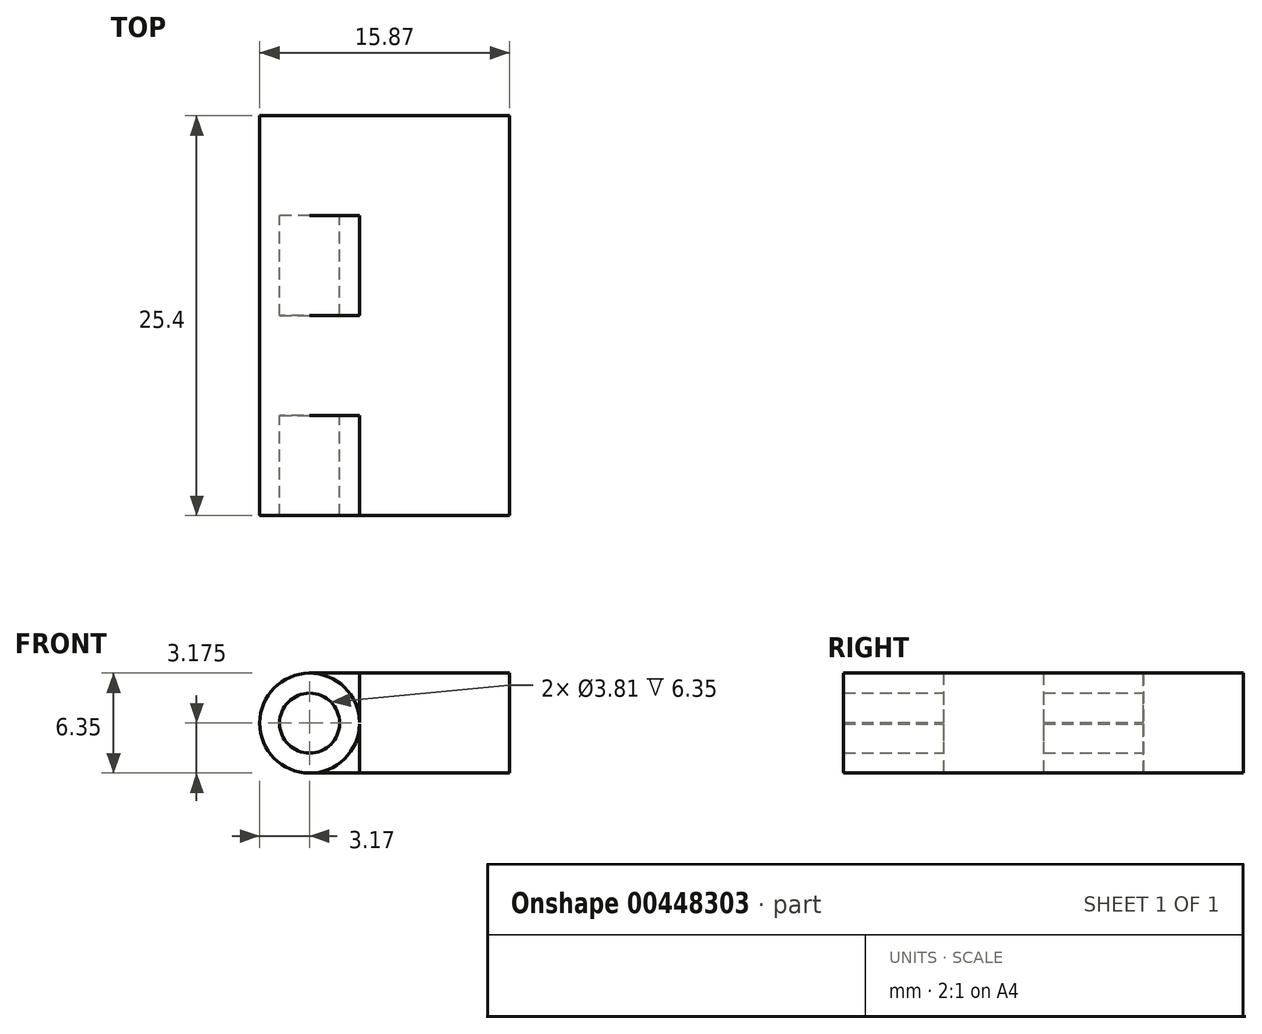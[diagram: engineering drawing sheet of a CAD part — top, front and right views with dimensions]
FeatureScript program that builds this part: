
annotation { "Feature Type Name" : "Feature", "Feature Type Description" : "" }
export const myFeature = defineFeature(function(context is Context, id is Id, definition is map)
    precondition{}
    {
        {
            var Q0;
            Q0=qCreatedBy(makeId("Top.planeOp"),FACE);
            var sketch = newSketch(context, id + "F0", { "sketchPlane" : qUnion([Q0])});
            skLineSegment(sketch, "E0.bottom", {"start": v(6.35, -12.7) * mm, "end": v(-6.35, -12.7) * mm});
            skLineSegment(sketch, "E0.top", {"start": v(6.35, 12.7) * mm, "end": v(-6.35, 12.7) * mm});
            skLineSegment(sketch, "E0.left", {"start": v(6.35, -12.7) * mm, "end": v(6.35, 12.7) * mm});
            skLineSegment(sketch, "E0.right", {"start": v(-6.35, -12.7) * mm, "end": v(-6.35, 12.7) * mm});
            skPoint(sketch, "E0.middle", {"position": v(0, 0) * mm});
            skSolve(sketch);
        }
        {
            var Q0;
            Q0=qSketchRegion(id+"F0",true);
            extrude(context, id + "F1", {"entities" : qUnion([Q0]), "depth" : 6.35 * mm});
        }
        {
            var Q0;
            Q0=makeQuery(id+"F1.opExtrude","SWEPT_FACE",FACE,{"disambiguationData":[OSD([sQuery(id+"F0.wireOp",EDGE,"E0.top")])]});
            var sketch = newSketch(context, id + "F2", { "sketchPlane" : qUnion([Q0])});
            skCircle(sketch, "E1", {"center": v(-6.35, 3.18) * mm, "radius": 3.17 * mm});
            skCircle(sketch, "E2", {"center": v(-6.35, 3.18) * mm, "radius": 1.9 * mm});
            skCircle(sketch, "E3.MirrorC", {"center": v(6.35, 3.18) * mm, "radius": 3.17 * mm});
            skCircle(sketch, "E4.MirrorC", {"center": v(6.35, 3.18) * mm, "radius": 1.9 * mm});
            skSolve(sketch);
        }
        {
            var Q0;
            {var subQ1=sQuery(id+"F0.wireOp",EDGE,"E0.top");var subQ2=makeQuery(id+"F1.opExtrude","SWEPT_EDGE",EDGE,{"disambiguationData":[OSD([subQ1,sQuery(id+"F0.wireOp",EDGE,"E0.right")])]});var subQ5=sQuery(id+"F2.wireOp",EDGE,"E4.MirrorC");var subQ7=makeQuery(id+"F2.imprint","INTERSECT",VERTEX,{"disambiguationData":[OD(0.0)],"derivedFrom":[subQ2,subQ5]});Q0=makeQuery(id+"F2.imprint","IMPRINT",FACE,{"disambiguationData":[TD([[makeQuery(id+"F2.imprint","IMPRINT",EDGE,{"disambiguationData":[TD([[subQ7,1.0]])],"derivedFrom":subQ5}),1.0]])]});}
            var Q1;
            {var subQ1=sQuery(id+"F0.wireOp",EDGE,"E0.top");var subQ2=makeQuery(id+"F1.opExtrude","SWEPT_EDGE",EDGE,{"disambiguationData":[OSD([subQ1,sQuery(id+"F0.wireOp",EDGE,"E0.left")])]});var subQ5=sQuery(id+"F2.wireOp",EDGE,"E2");var subQ7=makeQuery(id+"F2.imprint","INTERSECT",VERTEX,{"disambiguationData":[OD(0.0)],"derivedFrom":[subQ2,subQ5]});Q1=makeQuery(id+"F2.imprint","IMPRINT",FACE,{"disambiguationData":[TD([[makeQuery(id+"F2.imprint","IMPRINT",EDGE,{"disambiguationData":[TD([[subQ7,-1.0]])],"derivedFrom":subQ5}),-1.0]])]});}
            var Q2;
            {var subQ1=sQuery(id+"F0.wireOp",EDGE,"E0.top");var subQ2=makeQuery(id+"F1.opExtrude","SWEPT_EDGE",EDGE,{"disambiguationData":[OSD([subQ1,sQuery(id+"F0.wireOp",EDGE,"E0.right")])]});var subQ5=sQuery(id+"F2.wireOp",EDGE,"E4.MirrorC");var subQ6=makeQuery(id+"F2.imprint","INTERSECT",VERTEX,{"disambiguationData":[OD(0.0)],"derivedFrom":[subQ2,subQ5]});Q2=makeQuery(id+"F2.imprint","IMPRINT",FACE,{"disambiguationData":[TD([[makeQuery(id+"F2.imprint","IMPRINT",EDGE,{"disambiguationData":[TD([[subQ6,-1.0]])],"derivedFrom":subQ5}),1.0]])]});}
            var Q3;
            {var subQ0=sQuery(id+"F2.wireOp",EDGE,"E2");var subQ1=makeQuery(id+"F1.opExtrude","SWEPT_EDGE",EDGE,{"disambiguationData":[OSD([sQuery(id+"F0.wireOp",EDGE,"E0.top"),sQuery(id+"F0.wireOp",EDGE,"E0.left")])]});var subQ2=makeQuery(id+"F2.imprint","INTERSECT",VERTEX,{"disambiguationData":[OD(0.0)],"derivedFrom":[subQ1,subQ0]});Q3=makeQuery(id+"F2.imprint","IMPRINT",FACE,{"disambiguationData":[TD([[makeQuery(id+"F2.imprint","IMPRINT",EDGE,{"disambiguationData":[TD([[subQ2,-1.0]])],"derivedFrom":subQ0}),1.0]])]});}
            extrude(context, id + "F3", {"entities" : qUnion([Q0, Q1, Q2, Q3]), "operationType" : NewBodyOperationType.ADD, "oppositeDirection" : true, "depth" : 25.4 * mm});
        }
        {
            var Q0;
            {var subQ0=sQuery(id+"F2.wireOp",EDGE,"E2");var subQ1=makeQuery(id+"F1.opExtrude","SWEPT_EDGE",EDGE,{"disambiguationData":[OSD([sQuery(id+"F0.wireOp",EDGE,"E0.top"),sQuery(id+"F0.wireOp",EDGE,"E0.left")])]});var subQ2=makeQuery(id+"F2.imprint","INTERSECT",VERTEX,{"disambiguationData":[OD(0.0)],"derivedFrom":[subQ1,subQ0]});Q0=makeQuery(id+"F2.imprint","IMPRINT",FACE,{"disambiguationData":[TD([[makeQuery(id+"F2.imprint","IMPRINT",EDGE,{"disambiguationData":[TD([[subQ2,1.0]])],"derivedFrom":subQ0}),1.0]])]});}
            var Q1;
            {var subQ0=sQuery(id+"F2.wireOp",EDGE,"E4.MirrorC");var subQ1=makeQuery(id+"F1.opExtrude","SWEPT_EDGE",EDGE,{"disambiguationData":[OSD([sQuery(id+"F0.wireOp",EDGE,"E0.top"),sQuery(id+"F0.wireOp",EDGE,"E0.right")])]});var subQ2=makeQuery(id+"F2.imprint","INTERSECT",VERTEX,{"disambiguationData":[OD(0.0)],"derivedFrom":[subQ1,subQ0]});Q1=makeQuery(id+"F2.imprint","IMPRINT",FACE,{"disambiguationData":[TD([[makeQuery(id+"F2.imprint","IMPRINT",EDGE,{"disambiguationData":[TD([[subQ2,-1.0]])],"derivedFrom":subQ0}),-1.0]])]});}
            extrude(context, id + "F4", {"entities" : qUnion([Q0, Q1]), "operationType" : NewBodyOperationType.REMOVE, "oppositeDirection" : true, "depth" : 25.4 * mm});
        }
        {
            var Q0;
            Q0=makeQuery(id+"F1.opExtrude","CAP_FACE",FACE,{"disambiguationData":[OSD([sQuery(id+"F0.wireOp",EDGE,"E0.bottom"),sQuery(id+"F0.wireOp",EDGE,"E0.top"),sQuery(id+"F0.wireOp",EDGE,"E0.left"),sQuery(id+"F0.wireOp",EDGE,"E0.right")])],"isStart":true});
            var sketch = newSketch(context, id + "F5", { "sketchPlane" : qUnion([Q0])});
            skPoint(sketch, "E5.middle", {"position": v(6.35, 9.52) * mm});
            skLineSegment(sketch, "E6.MirrorCS", {"start": v(3.18, -12.7) * mm, "end": v(3.18, -6.35) * mm});
            skLineSegment(sketch, "E7.MirrorCS", {"start": v(9.53, -12.7) * mm, "end": v(9.53, -6.35) * mm});
            skLineSegment(sketch, "E8.MirrorCS", {"start": v(9.52, -12.7) * mm, "end": v(3.18, -12.7) * mm});
            skLineSegment(sketch, "E9", {"start": v(3.18, -6.35) * mm, "end": v(9.53, -6.35) * mm});
            skPoint(sketch, "E10.firstSnap0", {"position": v(6.35, 0) * mm});
            skLineSegment(sketch, "E10.bottom", {"start": v(9.53, 0) * mm, "end": v(3.18, 0) * mm});
            skLineSegment(sketch, "E10.top", {"start": v(9.53, 6.35) * mm, "end": v(3.18, 6.35) * mm});
            skLineSegment(sketch, "E10.left", {"start": v(9.53, 0) * mm, "end": v(9.53, 6.35) * mm});
            skLineSegment(sketch, "E10.right", {"start": v(3.18, 0) * mm, "end": v(3.18, 6.35) * mm});
            skLineSegment(sketch, "E11.top", {"start": v(3.18, -12.7) * mm, "end": v(9.53, -12.7) * mm});
            skLineSegment(sketch, "E11.left", {"start": v(3.18, -6.35) * mm, "end": v(3.18, -12.7) * mm});
            skLineSegment(sketch, "E11.right", {"start": v(9.53, -6.35) * mm, "end": v(9.53, -12.7) * mm});
            skLineSegment(sketch, "E12.MirrorCS", {"start": v(-9.53, 6.35) * mm, "end": v(-3.18, 6.35) * mm});
            skLineSegment(sketch, "E13.MirrorCS", {"start": v(-9.53, 0) * mm, "end": v(-3.18, 0) * mm});
            skLineSegment(sketch, "E14.MirrorCS", {"start": v(-3.18, -6.35) * mm, "end": v(-9.53, -6.35) * mm});
            skLineSegment(sketch, "E15.MirrorCS", {"start": v(-3.18, -6.35) * mm, "end": v(-3.18, 0) * mm});
            skLineSegment(sketch, "E16.MirrorCS", {"start": v(-9.53, -6.35) * mm, "end": v(-9.53, 0) * mm});
            skLineSegment(sketch, "E17.MirrorCS", {"start": v(-3.18, 0) * mm, "end": v(-9.53, 0) * mm});
            skLineSegment(sketch, "E18.MirrorCS", {"start": v(-3.18, 12.7) * mm, "end": v(-3.18, 6.35) * mm});
            skLineSegment(sketch, "E19.MirrorCS", {"start": v(-9.53, 12.7) * mm, "end": v(-9.53, 6.35) * mm});
            skLineSegment(sketch, "E20.MirrorCS", {"start": v(-9.53, 12.7) * mm, "end": v(-3.18, 12.7) * mm});
            skSolve(sketch);
        }
        {
            var Q0;
            {var subQ0=sQuery(id+"F5.wireOp",EDGE,"E19.MirrorCS");Q0=makeQuery(id+"F5.imprint","IMPRINT",FACE,{"disambiguationData":[TD([[makeQuery(id+"F5.imprint","IMPRINT",EDGE,{"derivedFrom":subQ0}),1.0]])]});}
            var Q1;
            {var subQ0=sQuery(id+"F5.wireOp",EDGE,"E16.MirrorCS");Q1=makeQuery(id+"F5.imprint","IMPRINT",FACE,{"disambiguationData":[TD([[makeQuery(id+"F5.imprint","IMPRINT",EDGE,{"derivedFrom":subQ0}),-1.0]])]});}
            var Q2;
            {var subQ0=sQuery(id+"F5.wireOp",EDGE,"E18.MirrorCS");Q2=makeQuery(id+"F5.imprint","IMPRINT",FACE,{"disambiguationData":[TD([[makeQuery(id+"F5.imprint","IMPRINT",EDGE,{"derivedFrom":subQ0}),-1.0]])]});}
            var Q3;
            {var subQ0=sQuery(id+"F5.wireOp",EDGE,"E15.MirrorCS");Q3=makeQuery(id+"F5.imprint","IMPRINT",FACE,{"disambiguationData":[TD([[makeQuery(id+"F5.imprint","IMPRINT",EDGE,{"derivedFrom":subQ0}),1.0]])]});}
            extrude(context, id + "F6", {"entities" : qUnion([Q0, Q1, Q2, Q3]), "operationType" : NewBodyOperationType.REMOVE, "oppositeDirection" : true, "depth" : 25.4 * mm});
        }
        {
            var Q0;
            {var subQ0=sQuery(id+"F2.wireOp",EDGE,"E4.MirrorC");var subQ1=makeQuery(id+"F1.opExtrude","SWEPT_EDGE",EDGE,{"disambiguationData":[OSD([sQuery(id+"F0.wireOp",EDGE,"E0.top"),sQuery(id+"F0.wireOp",EDGE,"E0.right")])]});var subQ2=makeQuery(id+"F2.imprint","INTERSECT",VERTEX,{"disambiguationData":[OD(0.0)],"derivedFrom":[subQ1,subQ0]});Q0=makeQuery(id+"F2.imprint","IMPRINT",FACE,{"disambiguationData":[TD([[makeQuery(id+"F2.imprint","IMPRINT",EDGE,{"disambiguationData":[TD([[subQ2,-1.0]])],"derivedFrom":subQ0}),-1.0]])]});}
            var Q1;
            {var subQ0=sQuery(id+"F2.wireOp",EDGE,"E4.MirrorC");var subQ1=makeQuery(id+"F1.opExtrude","SWEPT_EDGE",EDGE,{"disambiguationData":[OSD([sQuery(id+"F0.wireOp",EDGE,"E0.top"),sQuery(id+"F0.wireOp",EDGE,"E0.right")])]});var subQ2=makeQuery(id+"F2.imprint","INTERSECT",VERTEX,{"disambiguationData":[OD(0.0)],"derivedFrom":[subQ1,subQ0]});Q1=makeQuery(id+"F2.imprint","IMPRINT",FACE,{"disambiguationData":[TD([[makeQuery(id+"F2.imprint","IMPRINT",EDGE,{"disambiguationData":[TD([[subQ2,1.0]])],"derivedFrom":subQ0}),-1.0]])]});}
            extrude(context, id + "F7", {"entities" : qUnion([Q0, Q1]), "operationType" : NewBodyOperationType.ADD, "oppositeDirection" : true, "depth" : 25.4 * mm});
        }
    });
